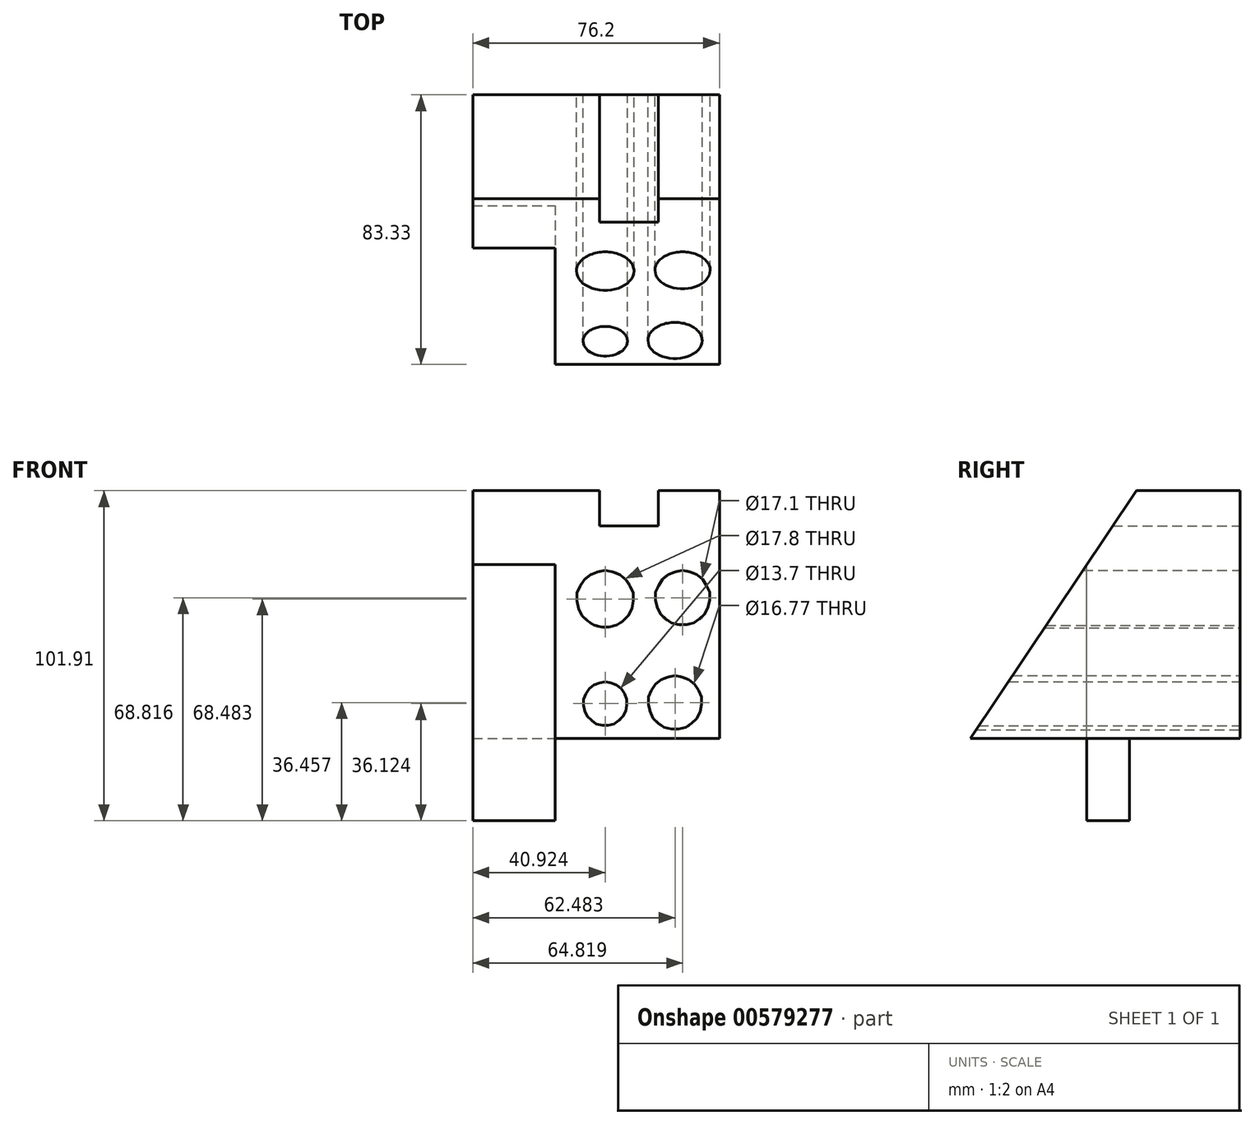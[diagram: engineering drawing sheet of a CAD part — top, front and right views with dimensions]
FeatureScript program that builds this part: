
annotation { "Feature Type Name" : "Feature", "Feature Type Description" : "" }
export const myFeature = defineFeature(function(context is Context, id is Id, definition is map)
    precondition{}
    {
        {
            var Q0;
            Q0=qCreatedBy(makeId("Right.planeOp"),FACE);
            var sketch = newSketch(context, id + "F0", { "sketchPlane" : qUnion([Q0])});
            skLineSegment(sketch, "E0", {"start": v(37.15, -24.98) * mm, "end": v(37.15, 51.53) * mm});
            skLineSegment(sketch, "E1", {"start": v(37.15, 51.53) * mm, "end": v(5.07, 51.53) * mm});
            skLineSegment(sketch, "E2", {"start": v(5.07, 51.53) * mm, "end": v(-46.18, -24.98) * mm});
            skLineSegment(sketch, "E3", {"start": v(-46.18, -24.98) * mm, "end": v(37.15, -24.98) * mm});
            skSolve(sketch);
        }
        {
            var Q0;
            Q0=makeQuery(id+"F0.imprint","IMPRINT",FACE,{"disambiguationData":[TD([[makeQuery(id+"F0.imprint","IMPRINT",EDGE,{"derivedFrom":sQuery(id+"F0.wireOp",EDGE,"E0")}),1.0]])]});
            extrude(context, id + "F1", {"entities" : qUnion([Q0]), "depth" : 50.8 * mm, "offsetDistance" : 25.4 * mm});
        }
        {
            var Q0;
            Q0=makeQuery(id+"F1.opExtrude","SWEPT_FACE",FACE,{"disambiguationData":[OSD([sQuery(id+"F0.wireOp",EDGE,"E0")])]});
            var sketch = newSketch(context, id + "F2", { "sketchPlane" : qUnion([Q0])});
            skLineSegment(sketch, "E4.bottom", {"start": v(-13.76, 51.53) * mm, "end": v(-32, 51.53) * mm});
            skLineSegment(sketch, "E4.top", {"start": v(-13.76, 40.67) * mm, "end": v(-32, 40.67) * mm});
            skLineSegment(sketch, "E4.left", {"start": v(-13.76, 51.53) * mm, "end": v(-13.76, 40.67) * mm});
            skLineSegment(sketch, "E4.right", {"start": v(-32, 51.53) * mm, "end": v(-32, 40.67) * mm});
            skSolve(sketch);
        }
        {
            var Q0;
            Q0=makeQuery(id+"F2.imprint","IMPRINT",FACE,{"disambiguationData":[TD([[makeQuery(id+"F2.imprint","IMPRINT",EDGE,{"derivedFrom":sQuery(id+"F2.wireOp",EDGE,"E4.bottom")}),-1.0]])]});
            extrude(context, id + "F3", {"entities" : qUnion([Q0]), "operationType" : NewBodyOperationType.REMOVE, "oppositeDirection" : true, "depth" : 63.5 * mm, "offsetDistance" : 25.4 * mm});
        }
        {
            var Q0;
            Q0=makeQuery(id+"F1.opExtrude","SWEPT_FACE",FACE,{"disambiguationData":[OSD([sQuery(id+"F0.wireOp",EDGE,"E0")])]});
            var sketch = newSketch(context, id + "F4", { "sketchPlane" : qUnion([Q0])});
            skCircle(sketch, "E5", {"center": v(-39.42, 18.44) * mm, "radius": 8.55 * mm});
            skCircle(sketch, "E6", {"center": v(-15.52, 18.1) * mm, "radius": 8.9 * mm});
            skCircle(sketch, "E7", {"center": v(-15.52, -14.26) * mm, "radius": 6.85 * mm});
            skCircle(sketch, "E8", {"center": v(-37.08, -13.92) * mm, "radius": 8.38 * mm});
            skSolve(sketch);
        }
        {
            var Q0;
            Q0=makeQuery(id+"F4.imprint","IMPRINT",FACE,{"disambiguationData":[TD([[makeQuery(id+"F4.imprint","IMPRINT",EDGE,{"derivedFrom":sQuery(id+"F4.wireOp",EDGE,"E5")}),1.0]])]});
            var Q1;
            Q1=makeQuery(id+"F4.imprint","IMPRINT",FACE,{"disambiguationData":[TD([[makeQuery(id+"F4.imprint","IMPRINT",EDGE,{"derivedFrom":sQuery(id+"F4.wireOp",EDGE,"E6")}),1.0]])]});
            var Q2;
            Q2=makeQuery(id+"F4.imprint","IMPRINT",FACE,{"disambiguationData":[TD([[makeQuery(id+"F4.imprint","IMPRINT",EDGE,{"derivedFrom":sQuery(id+"F4.wireOp",EDGE,"E7")}),1.0]])]});
            var Q3;
            Q3=makeQuery(id+"F4.imprint","IMPRINT",FACE,{"disambiguationData":[TD([[makeQuery(id+"F4.imprint","IMPRINT",EDGE,{"derivedFrom":sQuery(id+"F4.wireOp",EDGE,"E8")}),1.0]])]});
            extrude(context, id + "F5", {"entities" : qUnion([Q0, Q1, Q2, Q3]), "operationType" : NewBodyOperationType.REMOVE, "oppositeDirection" : true, "depth" : 109.47 * mm, "offsetDistance" : 25.4 * mm});
        }
        {
            var Q0;
            Q0=makeQuery(id+"F1.opExtrude","CAP_FACE",FACE,{"disambiguationData":[OSD([sQuery(id+"F0.wireOp",EDGE,"E0"),sQuery(id+"F0.wireOp",EDGE,"E1"),sQuery(id+"F0.wireOp",EDGE,"E2"),sQuery(id+"F0.wireOp",EDGE,"E3")])],"isStart":true});
            var sketch = newSketch(context, id + "F6", { "sketchPlane" : qUnion([Q0])});
            skLineSegment(sketch, "E9", {"start": v(-37.15, 51.53) * mm, "end": v(-37.15, -24.98) * mm});
            skLineSegment(sketch, "E10", {"start": v(-37.15, -24.98) * mm, "end": v(10.23, -24.98) * mm});
            skLineSegment(sketch, "E11", {"start": v(10.23, -24.98) * mm, "end": v(10.23, 28.68) * mm});
            skLineSegment(sketch, "E12", {"start": v(10.23, 28.68) * mm, "end": v(-5.07, 51.53) * mm});
            skLineSegment(sketch, "E13", {"start": v(-5.07, 51.53) * mm, "end": v(-37.15, 51.53) * mm});
            skSolve(sketch);
        }
        {
            var Q0;
            Q0=makeQuery(id+"F6.imprint","IMPRINT",FACE,{"disambiguationData":[TD([[makeQuery(id+"F6.imprint","IMPRINT",EDGE,{"derivedFrom":sQuery(id+"F6.wireOp",EDGE,"E9")}),-1.0]])]});
            extrude(context, id + "F7", {"entities" : qUnion([Q0]), "operationType" : NewBodyOperationType.ADD, "depth" : 25.4 * mm, "offsetDistance" : 25.4 * mm});
        }
        {
            var Q0;
            Q0=makeQuery(id+"F7.boolean.opBoolean","MERGE",FACE,{"derivedFrom":[makeQuery(id+"F1.opExtrude","SWEPT_FACE",FACE,{"disambiguationData":[OSD([sQuery(id+"F0.wireOp",EDGE,"E3")])]}),makeQuery(id+"F7.opExtrude","SWEPT_FACE",FACE,{"disambiguationData":[OSD([sQuery(id+"F6.wireOp",EDGE,"E10")])]})]});
            var sketch = newSketch(context, id + "F8", { "sketchPlane" : qUnion([Q0])});
            skLineSegment(sketch, "E14", {"start": v(-25.4, -2.9) * mm, "end": v(0, -2.9) * mm});
            skLineSegment(sketch, "E15", {"start": v(0, -2.9) * mm, "end": v(0, 10.23) * mm});
            skLineSegment(sketch, "E16", {"start": v(0, 10.23) * mm, "end": v(-21.74, 10.23) * mm});
            skLineSegment(sketch, "E17", {"start": v(-21.74, 10.23) * mm, "end": v(-25.4, 10.23) * mm});
            skLineSegment(sketch, "E18", {"start": v(-25.4, 10.23) * mm, "end": v(-25.4, -2.9) * mm});
            skSolve(sketch);
        }
        {
            var Q0;
            Q0=makeQuery(id+"F8.imprint","IMPRINT",FACE,{"disambiguationData":[TD([[makeQuery(id+"F8.imprint","IMPRINT",EDGE,{"derivedFrom":sQuery(id+"F8.wireOp",EDGE,"E14")}),1.0]])]});
            extrude(context, id + "F9", {"entities" : qUnion([Q0]), "operationType" : NewBodyOperationType.ADD, "depth" : 25.4 * mm, "offsetDistance" : 25.4 * mm});
        }
    });
